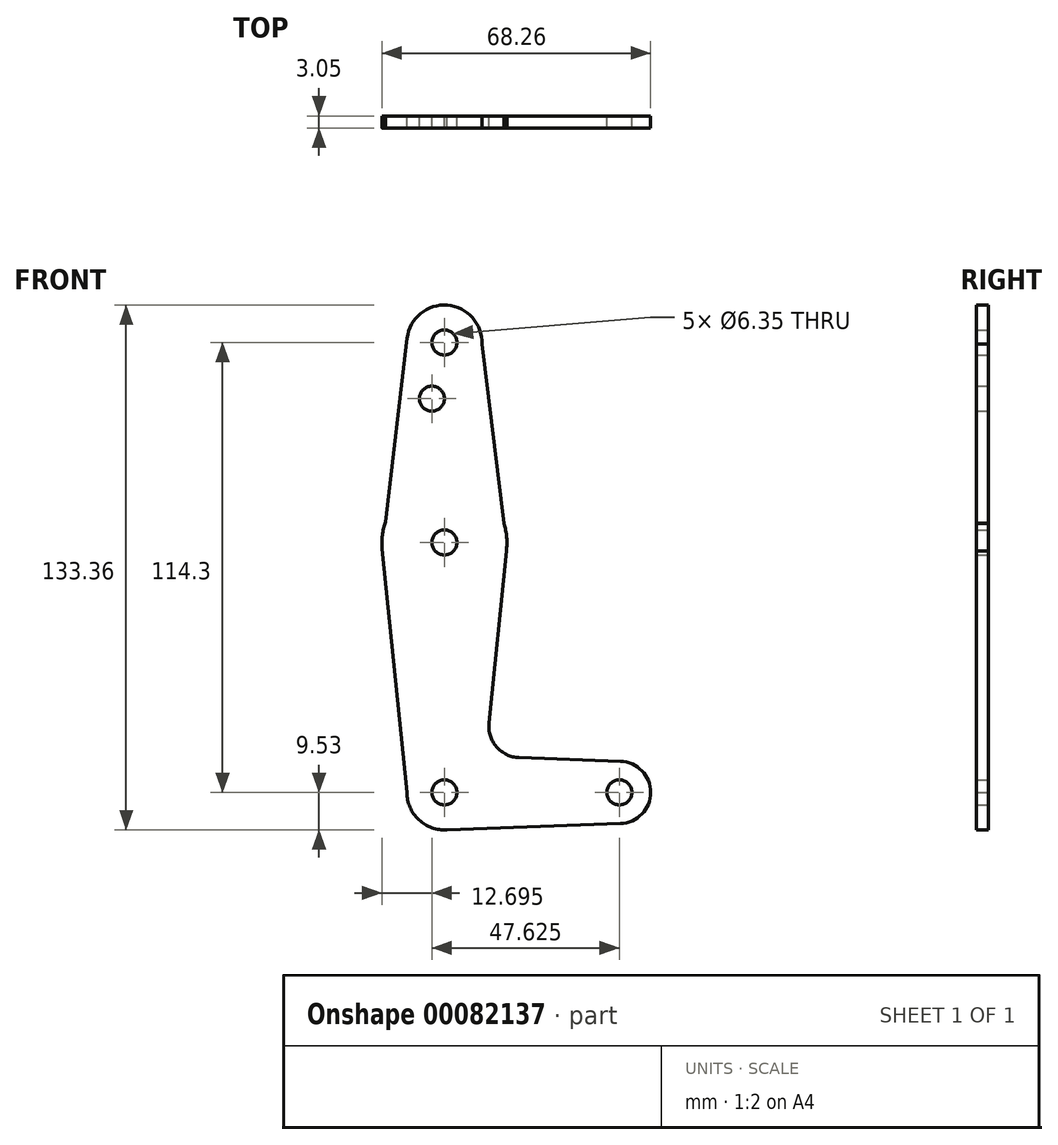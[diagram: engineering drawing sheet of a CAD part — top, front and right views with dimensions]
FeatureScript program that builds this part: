
annotation { "Feature Type Name" : "Feature", "Feature Type Description" : "" }
export const myFeature = defineFeature(function(context is Context, id is Id, definition is map)
    precondition{}
    {
        {
            var Q0;
            Q0=qCreatedBy(makeId("Front.planeOp"),FACE);
            var sketch = newSketch(context, id + "F0", { "sketchPlane" : qUnion([Q0])});
            skLineSegment(sketch, "E0", {"start": v(0, 0) * mm, "end": v(0, 114.3) * mm, "construction": true});
            skLineSegment(sketch, "E1", {"start": v(0, 0) * mm, "end": v(44.45, 0) * mm, "construction": true});
            skCircle(sketch, "E2", {"center": v(0, 114.3) * mm, "radius": 9.53 * mm});
            skCircle(sketch, "E3", {"center": v(0, 0) * mm, "radius": 9.53 * mm});
            skCircle(sketch, "E4", {"center": v(44.45, 0) * mm, "radius": 7.94 * mm});
            skCircle(sketch, "E5", {"center": v(0, 63.5) * mm, "radius": 15.88 * mm});
            skLineSegment(sketch, "E6", {"start": v(9.52, 113.89) * mm, "end": v(15.85, 62.55) * mm});
            skLineSegment(sketch, "E7", {"start": v(15.85, 62.55) * mm, "end": v(11.34, 17.59) * mm});
            skLineSegment(sketch, "E8", {"start": v(-9.53, 0) * mm, "end": v(-15.8, 61.9) * mm});
            skLineSegment(sketch, "E9", {"start": v(-15.8, 61.9) * mm, "end": v(-9.46, 115.42) * mm});
            skLineSegment(sketch, "E10", {"start": v(18.96, 8.85) * mm, "end": v(44.73, 7.93) * mm});
            skLineSegment(sketch, "E11", {"start": v(0, -9.53) * mm, "end": v(44.73, -7.93) * mm});
            skCircle(sketch, "E12", {"center": v(0, 114.3) * mm, "radius": 3.18 * mm});
            skCircle(sketch, "E13", {"center": v(0, 63.5) * mm, "radius": 3.18 * mm});
            skCircle(sketch, "E14", {"center": v(0, 0) * mm, "radius": 3.18 * mm});
            skCircle(sketch, "E15", {"center": v(44.45, 0) * mm, "radius": 3.18 * mm});
            skCircle(sketch, "E16", {"center": v(-3.18, 100.03) * mm, "radius": 3.18 * mm});
            skArc(sketch, "E17.filletArc", {"start": v(11.34, 17.59) * mm, "mid": v(13.26, 11.57) * mm, "end": v(18.96, 8.85) * mm});
            skSolve(sketch);
        }
        {
            var Q0;
            Q0 = qSketchRegion(id + "F0", true);
            extrude(context, id + "F1", {"entities" : qUnion([Q0]), "depth" : 3.05 * mm});
        }
    });
